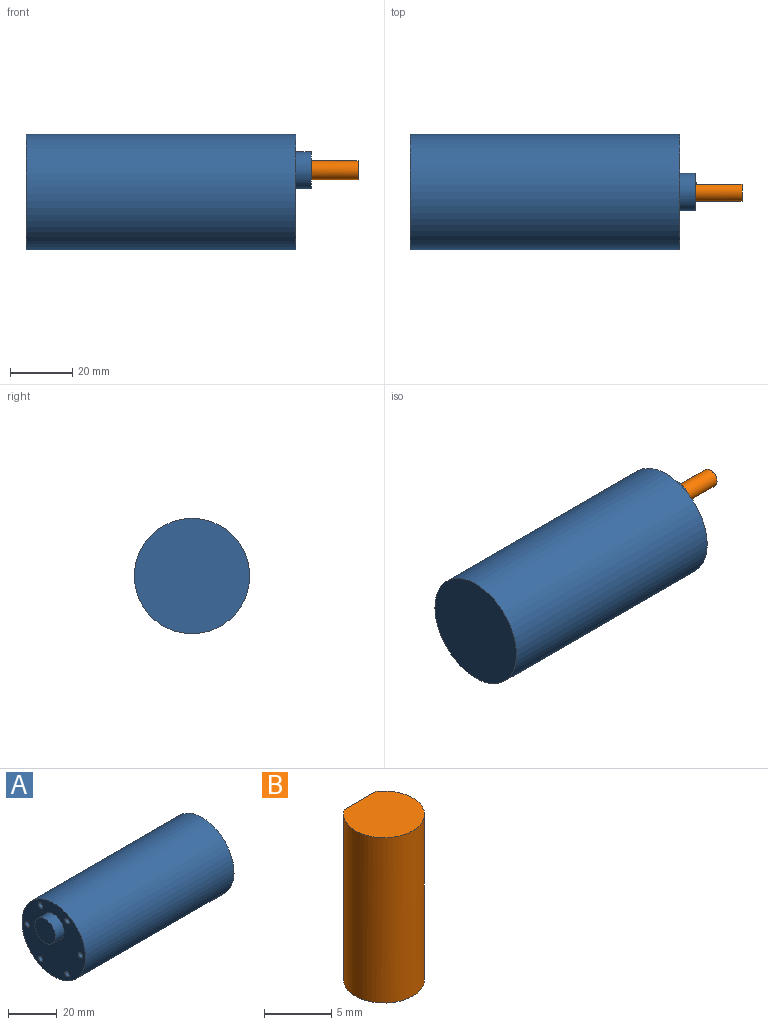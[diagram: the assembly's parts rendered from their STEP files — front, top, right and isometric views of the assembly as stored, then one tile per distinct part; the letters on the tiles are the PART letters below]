
ASSEMBLY  parts=2 mates=1
PART A: 17 faces, bbox 91.5x37x37 mm
  f0: plane 37x37mm, normal (-1,0,0), area 932.7mm2, adj f1,f3,f6,f8,f10,f12,f14,f16
  f1: cylinder r=18.5mm len=86.5mm, axis (-1,0,0), area 10054.7mm2, adj f0,f2
  f2: plane 37x37mm, normal (1,0,0), area 1075.2mm2, adj f1
  f3: cylinder r=6mm len=12mm, axis (1,0,0), area 188.5mm2, adj f0,f4
  f4: plane 12x12mm, normal (-1,0,0), area 113.1mm2, adj f3
  f5: cone r=0mm half-angle=59deg, axis (-1,0,0), area 5.7mm2, adj f6
  f6: cylinder r=1.25mm len=13.5mm, axis (-1,0,0), area 106mm2, adj f0,f5
  f7: cone r=0mm half-angle=59deg, axis (-1,0,0), area 5.7mm2, adj f8
  f8: cylinder r=1.25mm len=13.5mm, axis (-1,0,0), area 106mm2, adj f0,f7
  f9: cone r=0mm half-angle=59deg, axis (-1,0,0), area 5.7mm2, adj f10
  f10: cylinder r=1.25mm len=13.5mm, axis (-1,0,0), area 106mm2, adj f0,f9
  f11: cone r=0mm half-angle=59deg, axis (-1,0,0), area 5.7mm2, adj f12
  f12: cylinder r=1.25mm len=13.5mm, axis (-1,0,0), area 106mm2, adj f0,f11
  f13: cone r=0mm half-angle=59deg, axis (-1,0,0), area 5.7mm2, adj f14
  f14: cylinder r=1.25mm len=13.5mm, axis (-1,0,0), area 106mm2, adj f0,f13
  f15: cone r=0mm half-angle=59deg, axis (-1,0,0), area 5.7mm2, adj f16
  f16: cylinder r=1.25mm len=13.5mm, axis (-1,0,0), area 106mm2, adj f0,f15
PART B: 5 faces, bbox 6x6x15 mm
  f0: cylinder r=3mm len=15mm, axis (0,0,-1), area 231.8mm2, adj f1,f2,f3,f4
  f1: plane 6x5.5mm, normal (0,0,1), area 27.1mm2, adj f0,f4
  f2: plane 6x6mm, normal (0,0,-1), area 28.3mm2, adj f0
  f3: plane 3.32x0.5mm, normal (0,0,1), area 1.1mm2, adj f0,f4
  f4: plane 14.5x3.32mm, normal (0,1,0), area 48.1mm2, adj f0,f1,f3
PLACE A rot(axis=(0,0,-1),180deg) t=(66.01,-3.25,3.43)mm
PLACE B rot(axis=(0,1,0),90deg) t=(71.01,-3.25,10.43)mm
MATE revolute B.f0 <-> A.f3  axis (-1,0,0) through (71.01,-3.25,10.43)mm
